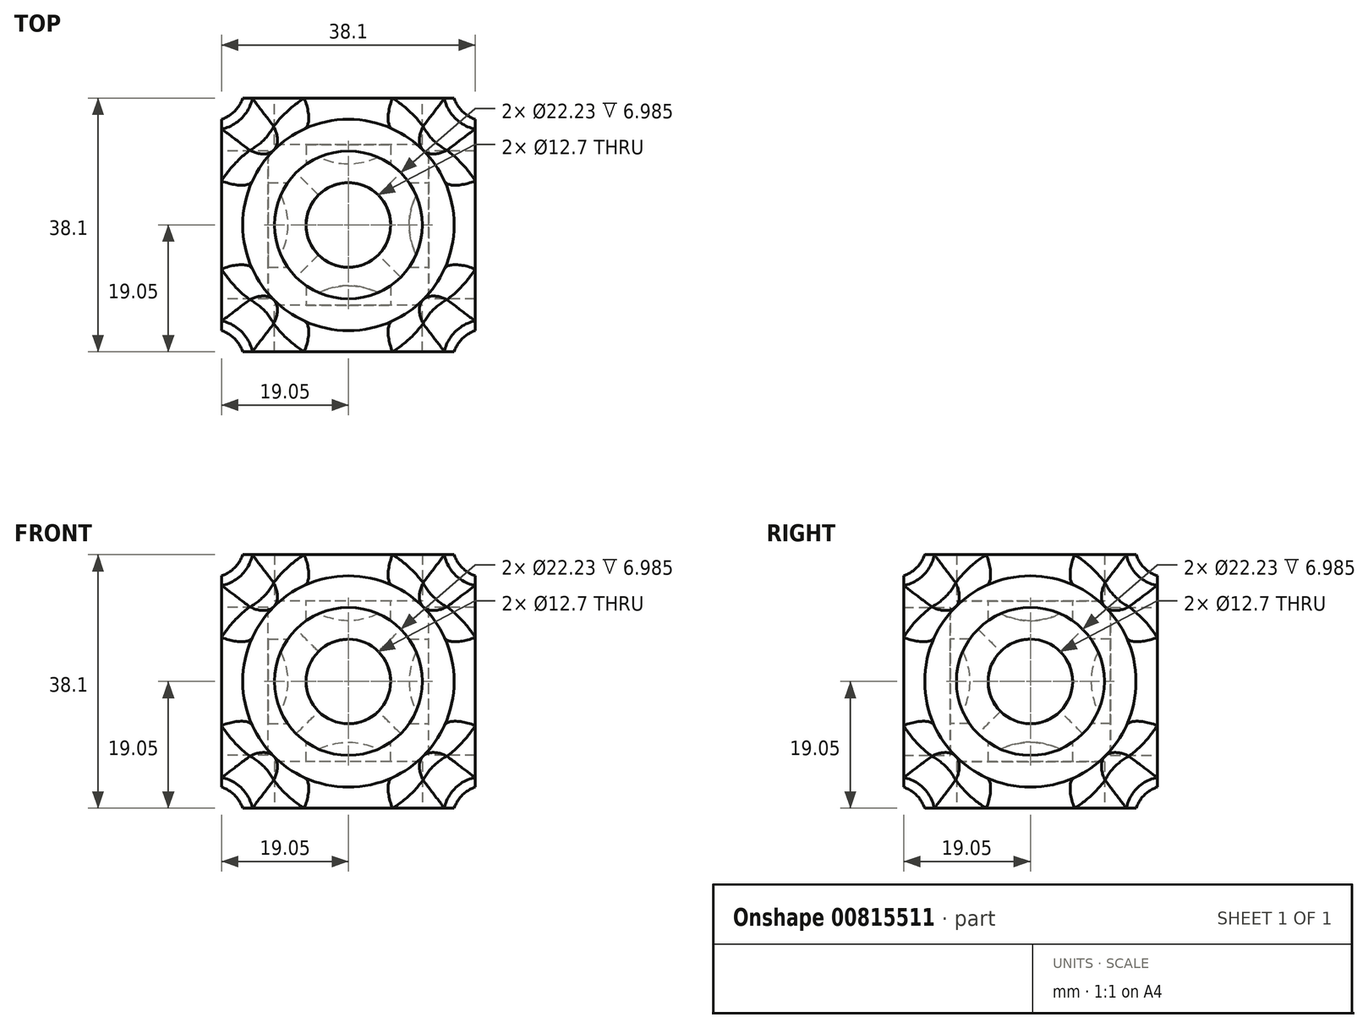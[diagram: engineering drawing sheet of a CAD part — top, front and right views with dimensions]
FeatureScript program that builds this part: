
annotation { "Feature Type Name" : "Feature", "Feature Type Description" : "" }
export const myFeature = defineFeature(function(context is Context, id is Id, definition is map)
    precondition{}
    {
        {
            var Q0;
            Q0=qCreatedBy(makeId("Top.planeOp"),FACE);
            var sketch = newSketch(context, id + "F0", { "sketchPlane" : qUnion([Q0])});
            skCircle(sketch, "E0", {"center": v(0, 0) * mm, "radius": 11.11 * mm});
            skCircle(sketch, "E1", {"center": v(0, 0) * mm, "radius": 15.88 * mm});
            skLineSegment(sketch, "E2", {"start": v(33.53, 0) * mm, "end": v(63.75, 0) * mm, "construction": true});
            skLineSegment(sketch, "E3", {"start": v(0, 32.1) * mm, "end": v(0, 51.95) * mm, "construction": true});
            skSolve(sketch);
        }
        {
            var Q0;
            Q0=makeQuery(id+"F0.imprint","IMPRINT",FACE,{"disambiguationData":[TD([[makeQuery(id+"F0.imprint","IMPRINT",EDGE,{"derivedFrom":sQuery(id+"F0.wireOp",EDGE,"E0")}),-1.0]])]});
            extrude(context, id + "F1", {"entities" : qUnion([Q0]), "depth" : 38.1 * mm, "offsetDistance" : 25.4 * mm});
        }
        {
            var Q0;
            Q0=makeQuery(id+"F1.opExtrude","SWEPT_BODY",BODY,{"disambiguationData":[OSD([sQuery(id+"F0.wireOp",EDGE,"E0"),sQuery(id+"F0.wireOp",EDGE,"E1")])]});
            transform(context, id + "F2", {"entities" : qUnion([Q0]), "transformType" : TransformType.TRANSLATION_3D, "dx" : 0 * mm, "dy" : 38.1 * mm, "dz" : 0 * mm, "makeCopy" : true});
        }
        {
            var Q0;
            Q0=makeQuery(id+"F2.opPattern","COPY",BODY,{"derivedFrom":makeQuery(id+"F1.opExtrude","SWEPT_BODY",BODY,{"disambiguationData":[OSD([sQuery(id+"F0.wireOp",EDGE,"E0"),sQuery(id+"F0.wireOp",EDGE,"E1")])]}),"instanceName":"1"});
            var Q1;
            Q1=sQuery(id+"F0.wireOp",EDGE,"E2");
            transform(context, id + "F3", {"entities" : qUnion([Q0]), "transformType" : TransformType.ROTATION, "transformAxis" : qUnion([Q1]), "angle" : 90 * degree, "makeCopy" : false});
        }
        {
            var Q0;
            Q0=makeQuery(id+"F2.opPattern","COPY",BODY,{"derivedFrom":makeQuery(id+"F1.opExtrude","SWEPT_BODY",BODY,{"disambiguationData":[OSD([sQuery(id+"F0.wireOp",EDGE,"E0"),sQuery(id+"F0.wireOp",EDGE,"E1")])]}),"instanceName":"1"});
            transform(context, id + "F4", {"entities" : qUnion([Q0]), "transformType" : TransformType.TRANSLATION_3D, "dx" : 0 * mm, "dy" : 19.05 * mm, "dz" : -19.05 * mm, "makeCopy" : false});
        }
        {
            var Q0;
            Q0=makeQuery(id+"F1.opExtrude","SWEPT_BODY",BODY,{"disambiguationData":[OSD([sQuery(id+"F0.wireOp",EDGE,"E0"),sQuery(id+"F0.wireOp",EDGE,"E1")])]});
            transform(context, id + "F5", {"entities" : qUnion([Q0]), "transformType" : TransformType.TRANSLATION_3D, "dx" : -38.1 * mm, "dy" : 0 * mm, "dz" : 0 * mm, "makeCopy" : true});
        }
        {
            var Q0;
            Q0=makeQuery(id+"F5.opPattern","COPY",BODY,{"derivedFrom":makeQuery(id+"F1.opExtrude","SWEPT_BODY",BODY,{"disambiguationData":[OSD([sQuery(id+"F0.wireOp",EDGE,"E0"),sQuery(id+"F0.wireOp",EDGE,"E1")])]}),"instanceName":"1"});
            var Q1;
            Q1=sQuery(id+"F0.wireOp",EDGE,"E3");
            transform(context, id + "F6", {"entities" : qUnion([Q0]), "transformType" : TransformType.ROTATION, "transformAxis" : qUnion([Q1]), "angle" : 90 * degree, "makeCopy" : false});
        }
        {
            var Q0;
            Q0=makeQuery(id+"F5.opPattern","COPY",BODY,{"derivedFrom":makeQuery(id+"F1.opExtrude","SWEPT_BODY",BODY,{"disambiguationData":[OSD([sQuery(id+"F0.wireOp",EDGE,"E0"),sQuery(id+"F0.wireOp",EDGE,"E1")])]}),"instanceName":"1"});
            transform(context, id + "F7", {"entities" : qUnion([Q0]), "transformType" : TransformType.TRANSLATION_3D, "dx" : -19.05 * mm, "dy" : 0 * mm, "dz" : -19.05 * mm, "makeCopy" : false});
        }
        {
            var Q0;
            Q0=makeQuery(id+"F2.opPattern","COPY",BODY,{"derivedFrom":makeQuery(id+"F1.opExtrude","SWEPT_BODY",BODY,{"disambiguationData":[OSD([sQuery(id+"F0.wireOp",EDGE,"E0"),sQuery(id+"F0.wireOp",EDGE,"E1")])]}),"instanceName":"1"});
            var Q1;
            Q1=makeQuery(id+"F5.opPattern","COPY",BODY,{"derivedFrom":makeQuery(id+"F1.opExtrude","SWEPT_BODY",BODY,{"disambiguationData":[OSD([sQuery(id+"F0.wireOp",EDGE,"E0"),sQuery(id+"F0.wireOp",EDGE,"E1")])]}),"instanceName":"1"});
            var Q2;
            Q2=makeQuery(id+"F1.opExtrude","SWEPT_BODY",BODY,{"disambiguationData":[OSD([sQuery(id+"F0.wireOp",EDGE,"E0"),sQuery(id+"F0.wireOp",EDGE,"E1")])]});
            booleanBodies(context, id + "F8", {"operationType" : BooleanOperationType.UNION, "tools" : qUnion([Q0, Q1, Q2])});
        }
        {
            var Q0;
            Q0=makeQuery(id+"F0.imprint","IMPRINT",FACE,{"disambiguationData":[TD([[makeQuery(id+"F0.imprint","IMPRINT",EDGE,{"derivedFrom":sQuery(id+"F0.wireOp",EDGE,"E0")}),1.0]])]});
            extrude(context, id + "F9", {"entities" : qUnion([Q0]), "operationType" : NewBodyOperationType.REMOVE, "depth" : 7 * mm, "offsetDistance" : 25.4 * mm});
        }
        {
            var Q0;
            Q0=makeQuery(id+"F5.opPattern","COPY",FACE,{"derivedFrom":makeQuery(id+"F1.opExtrude","CAP_FACE",FACE,{"disambiguationData":[OSD([sQuery(id+"F0.wireOp",EDGE,"E0"),sQuery(id+"F0.wireOp",EDGE,"E1")])],"isStart":true}),"instanceName":"1"});
            var sketch = newSketch(context, id + "F10", { "sketchPlane" : qUnion([Q0])});
            skCircle(sketch, "E4", {"center": v(0, 19.05) * mm, "radius": 11.11 * mm});
            skPoint(sketch, "E4.first.point", {"position": v(11.05, 20.18) * mm});
            skPoint(sketch, "E4.second.point", {"position": v(2.29, 29.92) * mm});
            skPoint(sketch, "E4.third.point", {"position": v(-10.47, 22.76) * mm});
            skSolve(sketch);
        }
        {
            var Q0;
            Q0=makeQuery(id+"F10.imprint","IMPRINT",FACE,{"disambiguationData":[TD([[makeQuery(id+"F10.imprint","IMPRINT",EDGE,{"derivedFrom":sQuery(id+"F10.wireOp",EDGE,"E4")}),-1.0]])]});
            extrude(context, id + "F11", {"entities" : qUnion([Q0]), "operationType" : NewBodyOperationType.REMOVE, "oppositeDirection" : true, "depth" : 7 * mm, "offsetDistance" : 25.4 * mm});
        }
        {
            var Q0;
            Q0=makeQuery(id+"F2.opPattern","COPY",FACE,{"derivedFrom":makeQuery(id+"F1.opExtrude","CAP_FACE",FACE,{"disambiguationData":[OSD([sQuery(id+"F0.wireOp",EDGE,"E0"),sQuery(id+"F0.wireOp",EDGE,"E1")])],"isStart":true}),"instanceName":"1"});
            var sketch = newSketch(context, id + "F12", { "sketchPlane" : qUnion([Q0])});
            skCircle(sketch, "E5", {"center": v(0, 19.05) * mm, "radius": 11.11 * mm});
            skPoint(sketch, "E5.first.point", {"position": v(10.14, 23.6) * mm});
            skPoint(sketch, "E5.second.point", {"position": v(-2.78, 29.8) * mm});
            skPoint(sketch, "E5.third.point", {"position": v(-10.76, 21.84) * mm});
            skSolve(sketch);
        }
        {
            var Q0;
            Q0=makeQuery(id+"F1.opExtrude","CAP_FACE",FACE,{"disambiguationData":[OSD([sQuery(id+"F0.wireOp",EDGE,"E0"),sQuery(id+"F0.wireOp",EDGE,"E1")])],"isStart":false});
            var sketch = newSketch(context, id + "F13", { "sketchPlane" : qUnion([Q0])});
            skCircle(sketch, "E6", {"center": v(0, 0) * mm, "radius": 11.11 * mm});
            skPoint(sketch, "E6.first.point", {"position": v(9.78, -5.28) * mm});
            skPoint(sketch, "E6.second.point", {"position": v(3.58, 10.52) * mm});
            skPoint(sketch, "E6.third.point", {"position": v(-8.53, 7.12) * mm});
            skCircle(sketch, "E7", {"center": v(0, 0) * mm, "radius": 6.35 * mm});
            skSolve(sketch);
        }
        {
            var Q0;
            Q0=makeQuery(id+"F2.opPattern","COPY",FACE,{"derivedFrom":makeQuery(id+"F1.opExtrude","CAP_FACE",FACE,{"disambiguationData":[OSD([sQuery(id+"F0.wireOp",EDGE,"E0"),sQuery(id+"F0.wireOp",EDGE,"E1")])],"isStart":false}),"instanceName":"1"});
            var sketch = newSketch(context, id + "F14", { "sketchPlane" : qUnion([Q0])});
            skCircle(sketch, "E8", {"center": v(0, 19.05) * mm, "radius": 11.11 * mm});
            skPoint(sketch, "E8.first.point", {"position": v(9.34, 13.03) * mm});
            skPoint(sketch, "E8.second.point", {"position": v(0, 30.16) * mm});
            skPoint(sketch, "E8.third.point", {"position": v(-9.05, 25.5) * mm});
            skCircle(sketch, "E9", {"center": v(0, 19.05) * mm, "radius": 6.35 * mm});
            skSolve(sketch);
        }
        {
            var Q0;
            Q0=makeQuery(id+"F5.opPattern","COPY",FACE,{"derivedFrom":makeQuery(id+"F1.opExtrude","CAP_FACE",FACE,{"disambiguationData":[OSD([sQuery(id+"F0.wireOp",EDGE,"E0"),sQuery(id+"F0.wireOp",EDGE,"E1")])],"isStart":false}),"instanceName":"1"});
            var sketch = newSketch(context, id + "F15", { "sketchPlane" : qUnion([Q0])});
            skCircle(sketch, "E10", {"center": v(0, 19.05) * mm, "radius": 11.11 * mm});
            skPoint(sketch, "E10.first.point", {"position": v(-10.74, 16.22) * mm});
            skPoint(sketch, "E10.second.point", {"position": v(3.5, 8.5) * mm});
            skPoint(sketch, "E10.third.point", {"position": v(9.9, 24.09) * mm});
            skCircle(sketch, "E11", {"center": v(0, 19.05) * mm, "radius": 6.35 * mm});
            skSolve(sketch);
        }
        {
            var Q0;
            Q0=makeQuery(id+"F15.imprint","IMPRINT",FACE,{"disambiguationData":[TD([[makeQuery(id+"F15.imprint","IMPRINT",EDGE,{"derivedFrom":sQuery(id+"F15.wireOp",EDGE,"E10")}),1.0]])]});
            var Q1;
            Q1=makeQuery(id+"F15.imprint","IMPRINT",FACE,{"disambiguationData":[TD([[makeQuery(id+"F15.imprint","IMPRINT",EDGE,{"derivedFrom":sQuery(id+"F15.wireOp",EDGE,"E11")}),1.0]])]});
            extrude(context, id + "F16", {"entities" : qUnion([Q0, Q1]), "operationType" : NewBodyOperationType.REMOVE, "oppositeDirection" : true, "depth" : 7 * mm, "offsetDistance" : 25.4 * mm});
        }
        {
            var Q0;
            Q0=makeQuery(id+"F14.imprint","IMPRINT",FACE,{"disambiguationData":[TD([[makeQuery(id+"F14.imprint","IMPRINT",EDGE,{"derivedFrom":sQuery(id+"F14.wireOp",EDGE,"E8")}),1.0]])]});
            var Q1;
            Q1=makeQuery(id+"F14.imprint","IMPRINT",FACE,{"disambiguationData":[TD([[makeQuery(id+"F14.imprint","IMPRINT",EDGE,{"derivedFrom":sQuery(id+"F14.wireOp",EDGE,"E9")}),1.0]])]});
            extrude(context, id + "F17", {"entities" : qUnion([Q0, Q1]), "operationType" : NewBodyOperationType.REMOVE, "oppositeDirection" : true, "depth" : 7 * mm, "offsetDistance" : 25.4 * mm});
        }
        {
            var Q0;
            Q0=makeQuery(id+"F13.imprint","IMPRINT",FACE,{"disambiguationData":[TD([[makeQuery(id+"F13.imprint","IMPRINT",EDGE,{"derivedFrom":sQuery(id+"F13.wireOp",EDGE,"E6")}),1.0]])]});
            var Q1;
            Q1=makeQuery(id+"F13.imprint","IMPRINT",FACE,{"disambiguationData":[TD([[makeQuery(id+"F13.imprint","IMPRINT",EDGE,{"derivedFrom":sQuery(id+"F13.wireOp",EDGE,"E7")}),1.0]])]});
            extrude(context, id + "F18", {"entities" : qUnion([Q0, Q1]), "operationType" : NewBodyOperationType.REMOVE, "oppositeDirection" : true, "depth" : 7 * mm, "offsetDistance" : 25.4 * mm});
        }
        {
            var Q0;
            Q0=makeQuery(id+"F12.imprint","IMPRINT",FACE,{"disambiguationData":[TD([[makeQuery(id+"F12.imprint","IMPRINT",EDGE,{"derivedFrom":sQuery(id+"F12.wireOp",EDGE,"E5")}),-1.0]])]});
            extrude(context, id + "F19", {"entities" : qUnion([Q0]), "operationType" : NewBodyOperationType.REMOVE, "oppositeDirection" : true, "depth" : 7 * mm, "offsetDistance" : 25.4 * mm});
        }
        {
            var Q0;
            {var subQ0=makeQuery(id+"F1.opExtrude","SWEPT_FACE",FACE,{"disambiguationData":[OSD([sQuery(id+"F0.wireOp",EDGE,"E1")])]});Q0=makeQuery(id+"F8.opBoolean","INTERSECT",EDGE,{"disambiguationData":[OD(3.0)],"derivedFrom":[subQ0,makeQuery(id+"F5.opPattern","COPY",FACE,{"derivedFrom":subQ0,"instanceName":"1"})]});}
            var Q1;
            {var subQ0=makeQuery(id+"F1.opExtrude","SWEPT_FACE",FACE,{"disambiguationData":[OSD([sQuery(id+"F0.wireOp",EDGE,"E1")])]});Q1=makeQuery(id+"F8.opBoolean","INTERSECT",EDGE,{"disambiguationData":[OD(1.0)],"derivedFrom":[makeQuery(id+"F2.opPattern","COPY",FACE,{"derivedFrom":subQ0,"instanceName":"1"}),makeQuery(id+"F5.opPattern","COPY",FACE,{"derivedFrom":subQ0,"instanceName":"1"})]});}
            var Q2;
            {var subQ0=makeQuery(id+"F1.opExtrude","SWEPT_FACE",FACE,{"disambiguationData":[OSD([sQuery(id+"F0.wireOp",EDGE,"E1")])]});Q2=makeQuery(id+"F8.opBoolean","INTERSECT",EDGE,{"disambiguationData":[OD(2.0)],"derivedFrom":[subQ0,makeQuery(id+"F2.opPattern","COPY",FACE,{"derivedFrom":subQ0,"instanceName":"1"})]});}
            var Q3;
            {var subQ0=makeQuery(id+"F1.opExtrude","SWEPT_FACE",FACE,{"disambiguationData":[OSD([sQuery(id+"F0.wireOp",EDGE,"E1")])]});Q3=makeQuery(id+"F8.opBoolean","INTERSECT",EDGE,{"disambiguationData":[OD(0.0)],"derivedFrom":[makeQuery(id+"F2.opPattern","COPY",FACE,{"derivedFrom":subQ0,"instanceName":"1"}),makeQuery(id+"F5.opPattern","COPY",FACE,{"derivedFrom":subQ0,"instanceName":"1"})]});}
            var Q4;
            {var subQ0=makeQuery(id+"F1.opExtrude","SWEPT_FACE",FACE,{"disambiguationData":[OSD([sQuery(id+"F0.wireOp",EDGE,"E1")])]});Q4=makeQuery(id+"F8.opBoolean","INTERSECT",EDGE,{"disambiguationData":[OD(2.0)],"derivedFrom":[subQ0,makeQuery(id+"F5.opPattern","COPY",FACE,{"derivedFrom":subQ0,"instanceName":"1"})]});}
            var Q5;
            {var subQ0=makeQuery(id+"F1.opExtrude","SWEPT_FACE",FACE,{"disambiguationData":[OSD([sQuery(id+"F0.wireOp",EDGE,"E1")])]});Q5=makeQuery(id+"F8.opBoolean","INTERSECT",EDGE,{"disambiguationData":[OD(3.0)],"derivedFrom":[subQ0,makeQuery(id+"F2.opPattern","COPY",FACE,{"derivedFrom":subQ0,"instanceName":"1"})]});}
            var Q6;
            {var subQ0=makeQuery(id+"F1.opExtrude","SWEPT_FACE",FACE,{"disambiguationData":[OSD([sQuery(id+"F0.wireOp",EDGE,"E1")])]});Q6=makeQuery(id+"F8.opBoolean","INTERSECT",EDGE,{"disambiguationData":[OD(2.0)],"derivedFrom":[makeQuery(id+"F2.opPattern","COPY",FACE,{"derivedFrom":subQ0,"instanceName":"1"}),makeQuery(id+"F5.opPattern","COPY",FACE,{"derivedFrom":subQ0,"instanceName":"1"})]});}
            var Q7;
            {var subQ0=makeQuery(id+"F1.opExtrude","SWEPT_FACE",FACE,{"disambiguationData":[OSD([sQuery(id+"F0.wireOp",EDGE,"E1")])]});Q7=makeQuery(id+"F8.opBoolean","INTERSECT",EDGE,{"disambiguationData":[OD(0.0)],"derivedFrom":[subQ0,makeQuery(id+"F5.opPattern","COPY",FACE,{"derivedFrom":subQ0,"instanceName":"1"})]});}
            var Q8;
            {var subQ0=makeQuery(id+"F1.opExtrude","SWEPT_FACE",FACE,{"disambiguationData":[OSD([sQuery(id+"F0.wireOp",EDGE,"E1")])]});Q8=makeQuery(id+"F8.opBoolean","INTERSECT",EDGE,{"disambiguationData":[OD(1.0)],"derivedFrom":[subQ0,makeQuery(id+"F2.opPattern","COPY",FACE,{"derivedFrom":subQ0,"instanceName":"1"})]});}
            var Q9;
            {var subQ0=makeQuery(id+"F1.opExtrude","SWEPT_FACE",FACE,{"disambiguationData":[OSD([sQuery(id+"F0.wireOp",EDGE,"E1")])]});Q9=makeQuery(id+"F8.opBoolean","INTERSECT",EDGE,{"disambiguationData":[OD(3.0)],"derivedFrom":[makeQuery(id+"F2.opPattern","COPY",FACE,{"derivedFrom":subQ0,"instanceName":"1"}),makeQuery(id+"F5.opPattern","COPY",FACE,{"derivedFrom":subQ0,"instanceName":"1"})]});}
            var Q10;
            {var subQ0=makeQuery(id+"F1.opExtrude","SWEPT_FACE",FACE,{"disambiguationData":[OSD([sQuery(id+"F0.wireOp",EDGE,"E1")])]});Q10=makeQuery(id+"F8.opBoolean","INTERSECT",EDGE,{"disambiguationData":[OD(1.0)],"derivedFrom":[subQ0,makeQuery(id+"F5.opPattern","COPY",FACE,{"derivedFrom":subQ0,"instanceName":"1"})]});}
            var Q11;
            {var subQ0=makeQuery(id+"F1.opExtrude","SWEPT_FACE",FACE,{"disambiguationData":[OSD([sQuery(id+"F0.wireOp",EDGE,"E1")])]});Q11=makeQuery(id+"F8.opBoolean","INTERSECT",EDGE,{"disambiguationData":[OD(0.0)],"derivedFrom":[subQ0,makeQuery(id+"F2.opPattern","COPY",FACE,{"derivedFrom":subQ0,"instanceName":"1"})]});}
            fillet(context, id + "F20", {"entities" : qUnion([Q0, Q1, Q2, Q3, Q4, Q5, Q6, Q7, Q8, Q9, Q10, Q11]), "radius" : 5.08 * mm, "tangentPropagation" : true, "allowEdgeOverflow" : false});
        }
        {
            var Q0;
            Q0=makeQuery(id+"F15.imprint","IMPRINT",FACE,{"disambiguationData":[TD([[makeQuery(id+"F15.imprint","IMPRINT",EDGE,{"derivedFrom":sQuery(id+"F15.wireOp",EDGE,"E11")}),1.0]])]});
            extrude(context, id + "F21", {"entities" : qUnion([Q0]), "operationType" : NewBodyOperationType.REMOVE, "endBound" : BoundingType.THROUGH_ALL, "oppositeDirection" : true, "depth" : 25.4 * mm, "offsetDistance" : 25.4 * mm});
        }
        {
            var Q0;
            Q0=makeQuery(id+"F14.imprint","IMPRINT",FACE,{"disambiguationData":[TD([[makeQuery(id+"F14.imprint","IMPRINT",EDGE,{"derivedFrom":sQuery(id+"F14.wireOp",EDGE,"E9")}),1.0]])]});
            extrude(context, id + "F22", {"entities" : qUnion([Q0]), "operationType" : NewBodyOperationType.REMOVE, "endBound" : BoundingType.THROUGH_ALL, "oppositeDirection" : true, "depth" : 25.4 * mm, "offsetDistance" : 25.4 * mm});
        }
        {
            var Q0;
            Q0=makeQuery(id+"F13.imprint","IMPRINT",FACE,{"disambiguationData":[TD([[makeQuery(id+"F13.imprint","IMPRINT",EDGE,{"derivedFrom":sQuery(id+"F13.wireOp",EDGE,"E7")}),1.0]])]});
            extrude(context, id + "F23", {"entities" : qUnion([Q0]), "operationType" : NewBodyOperationType.REMOVE, "endBound" : BoundingType.THROUGH_ALL, "oppositeDirection" : true, "depth" : 25.4 * mm, "offsetDistance" : 25.4 * mm});
        }
    });
